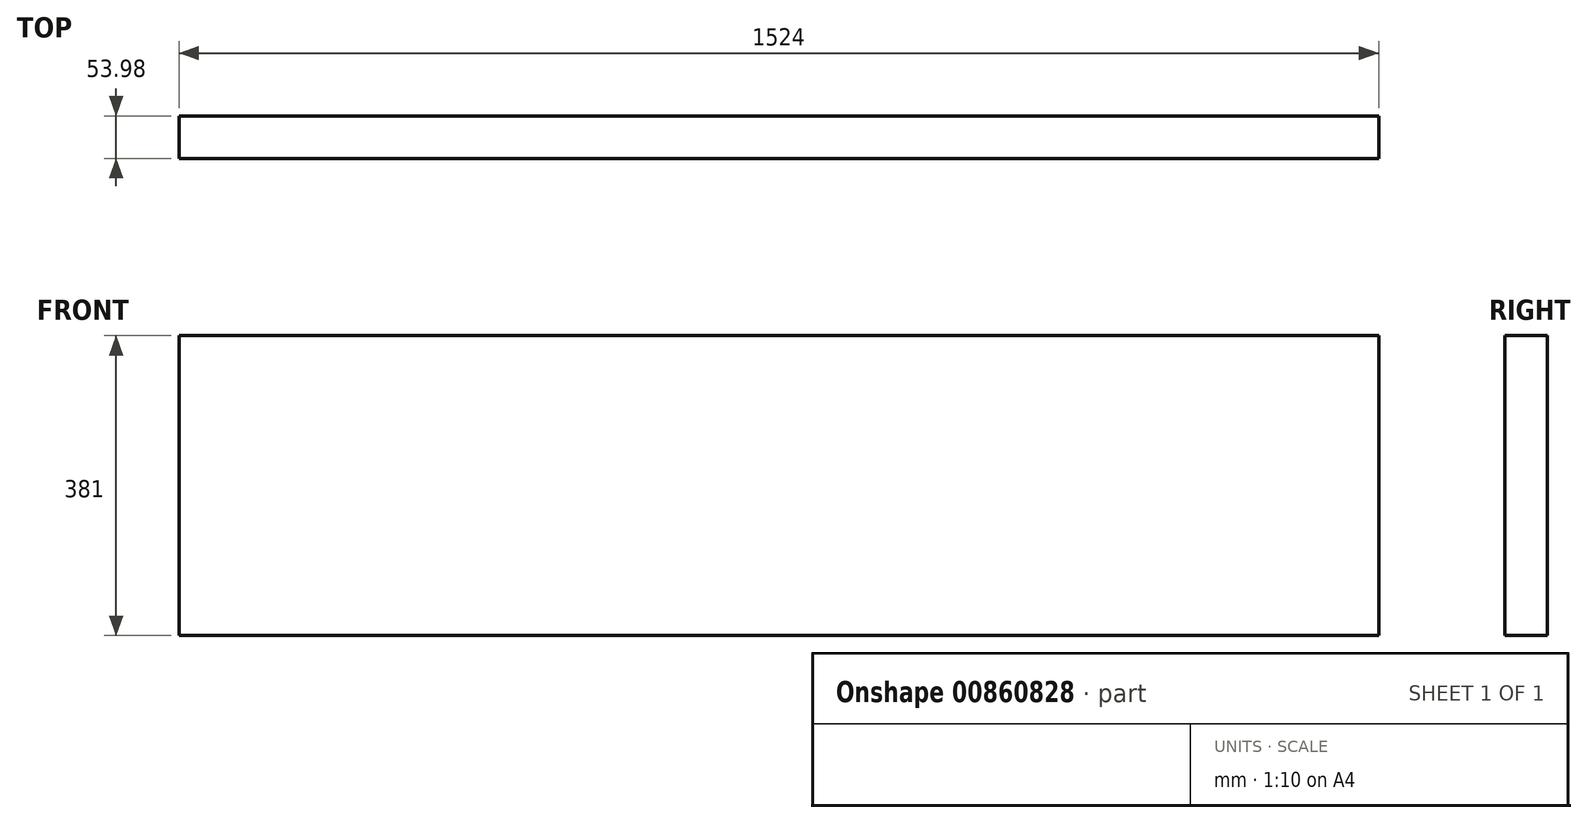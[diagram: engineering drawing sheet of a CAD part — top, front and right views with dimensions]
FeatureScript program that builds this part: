
annotation { "Feature Type Name" : "Feature", "Feature Type Description" : "" }
export const myFeature = defineFeature(function(context is Context, id is Id, definition is map)
    precondition{}
    {
        {
            var Q0;
            Q0=qCreatedBy(makeId("Front.planeOp"),FACE);
            var sketch = newSketch(context, id + "F0", { "sketchPlane" : qUnion([Q0])});
            skLineSegment(sketch, "E0", {"start": v(-1014.16, 255.2) * mm, "end": v(-1014.16, -125.8) * mm});
            skLineSegment(sketch, "E1", {"start": v(-1014.16, -125.8) * mm, "end": v(509.84, -125.8) * mm});
            skLineSegment(sketch, "E2", {"start": v(509.84, -125.8) * mm, "end": v(509.84, 255.2) * mm});
            skPoint(sketch, "E3.start.orphan", {"position": v(500.68, 255.2) * mm});
            skLineSegment(sketch, "E4", {"start": v(-1014.16, 255.2) * mm, "end": v(509.84, 255.2) * mm});
            skSolve(sketch);
        }
        {
            var Q0;
            Q0 = qSketchRegion(id + "F0", true);
            extrude(context, id + "F1", {"entities" : qUnion([Q0]), "depth" : 53.97 * mm, "offsetDistance" : 25.4 * mm});
        }
    });
